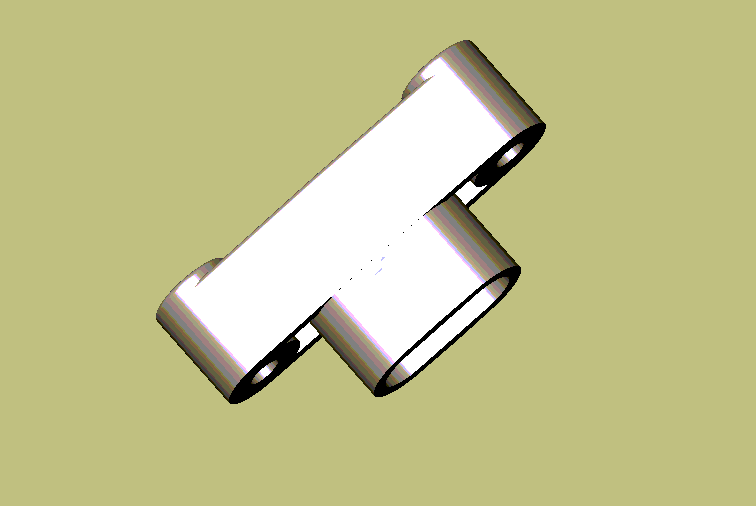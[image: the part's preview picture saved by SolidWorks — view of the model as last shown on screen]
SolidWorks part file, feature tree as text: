
SOLIDWORKS PART (.sldprt)
format: sldprt  version: not decoded by parser v0  size: 217,600 bytes
history: native  units: mm
features: sketch x8, shell x4, plane x3, cut_extrude x3, extrude x2, material x1, fillet x1 (+8 scaffold rows collapsed)
feature tree (30):
  scaffold x8  (default folders/planes/origin — collapsed)
  material  "Matériau <non spécifié>"
  plane  "Plane1"
  plane  "Plane2"
  plane  "Plane3"
  sketch  "Esquisse1"  dims[D1=8.0mm D2=28.0mm D3=4.5mm]
  extrude  "Base-Extrusion"  Depth=9mm
  sketch  "Esquisse2"
  extrude  "Boss.-Extru.1"  Depth=1mm
  fillet  "Congé2"  Radius=0.5mm
  shell  "Coque1"  Thickness=1.5mm
  sketch  "Esquisse3"
  shell  "Boss.-Extru.2"  [1 undecoded]
  sketch  "Esquisse4"
  shell  "Boss.-Extru.3"  [1 undecoded]
  sketch  "Esquisse5"  dims[D1=4.0mm D2=4.0mm]
  shell  "Boss.-Extru.4"  Thickness=15.5mm
  sketch  "Esquisse6"  dims[c1.D1=~7.211103mm c1.D2=~3.605551mm c2.D1=6.0mm c2.D2=6.0mm]
  cut_extrude  "Enlèv. mat.-Extru.1"  Depth=8mm
  sketch  "Esquisse7"  dims[D1=3.0mm D2=3.0mm D3=3.0mm D4=3.0mm]
  cut_extrude  "Enlèv. mat.-Extru.2"  [1 undecoded]
  sketch  "Esquisse8"  dims[D1=7.0mm D2=7.0mm]
  cut_extrude  "Enlèv. mat.-Extru.3"  Depth=8mm
decode coverage: 12 of 18 modeling features carry decoded parameters
note: ~ marks probable driven/reference dimensions
note: 3 parameter values undecoded
summary: no parameter record found for 3 features
note: suppression state not decoded; provenance and decode notes live in map.json
